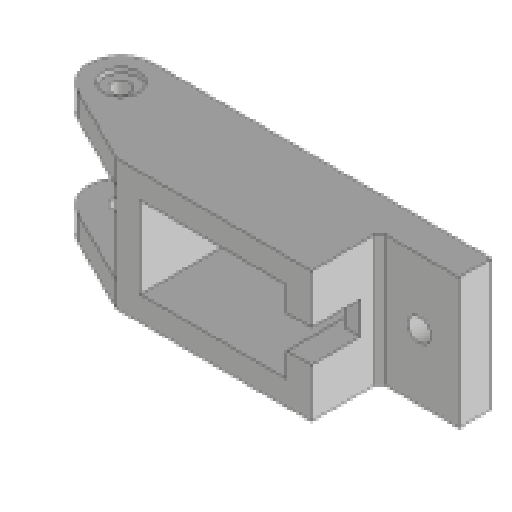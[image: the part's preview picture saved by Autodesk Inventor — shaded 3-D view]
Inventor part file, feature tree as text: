
AUTODESK INVENTOR PART (.ipt)
format: ipt  version: 2025 (Build 290162010, 162A)  size: 228,864 bytes
history: native  units: in
note: dims shown in document units (in); Inventor stores cm internally (conversion verified against a paired STEP export)
features: extrude x9, sketch x9, plane x2, mirror x2, chamfer x1, projected_geometry x1
ambient origin geometry x8: Origin, YZ Plane, XZ Plane, XY Plane, X Axis, Y Axis, Z Axis, Center Point
bodies: Solid1 (feature_tree)
feature tree (24):
  extrude  "Extrusion1"  Depth=0.5in
  extrude  "Extrusion2"  Depth=0.618in TaperAngle=0.0deg
  extrude  "Extrusion3"  Depth=0.3in
  chamfer  "Chamfer1"  Distance=0.618in
  extrude  "Extrusion4"  Depth=0.2in TaperAngle=0.0deg
  plane  "Work Plane1"
  extrude  "Extrusion5"  Depth=0.07in
  plane  "Work Plane2"
  mirror  "Mirror1"
  extrude  "Extrusion6"  Depth=0.187in
  mirror  "Mirror2"
  extrude  "Extrusion7"  Depth=0.2in
  extrude  "Extrusion8"  Depth=0.11in
  extrude  "Extrusion9"  Depth=0.1in
  sketch  "Sketch1"  dims[d0=0.9in d1=0.5in]
  sketch  "Sketch2"  dims[d2=0.8in d3=0.618in d4=0.0in]
  sketch  "Sketch3"  dims[d5=0.2in d6=0.3in d7=0.618in d8=0.0in]
  sketch  "Sketch4"  dims[d9=0.187in d10=0.2in d11=0.0in]
  sketch  "Sketch5"  dims[d12=0.037in d13=0.125in d14=45.0deg d15=0.07in]
  sketch  "Sketch6"  dims[d16=0.3in d17=0.0in d18=0.187in]
  sketch  "Sketch7"  dims[d21=0.15in d22=0.0in d24=0.2in]
  projected_geometry  "Projected Loop1"
  sketch  "Sketch8"  dims[d25=0.35in d26=0.11in]
  sketch  "Sketch9"  dims[d27=0.55in d29=0.22in d30=0.03in d31=0.0in d32=0.45in d33=0.0in d34=0.14in d35=0.7375in d36=0.0in d37=0.2in d38=0.055in d39=0.1in d40=0.875in d41=0.0in d42=0.6in]
